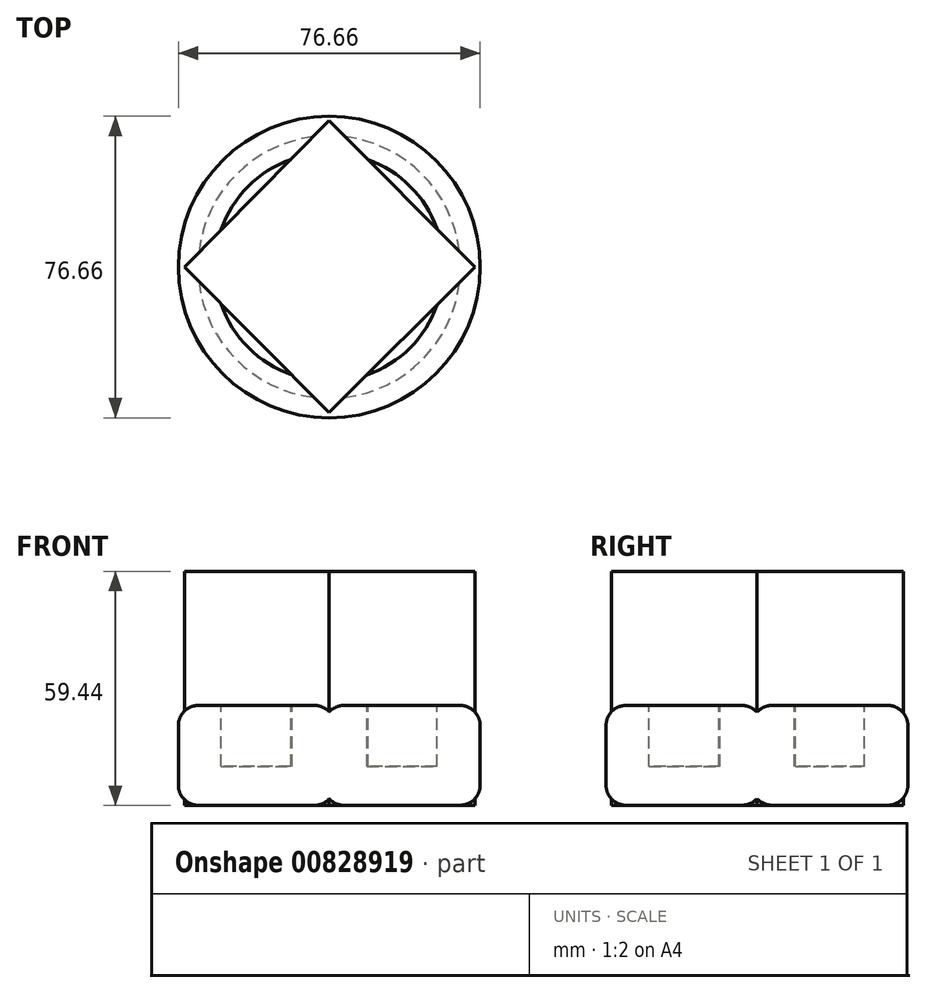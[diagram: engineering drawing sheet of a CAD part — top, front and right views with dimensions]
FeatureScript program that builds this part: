
annotation { "Feature Type Name" : "Feature", "Feature Type Description" : "" }
export const myFeature = defineFeature(function(context is Context, id is Id, definition is map)
    precondition{}
    {
        {
            var Q0;
            Q0=qCreatedBy(makeId("Top.planeOp"),FACE);
            var sketch = newSketch(context, id + "F0", { "sketchPlane" : qUnion([Q0])});
            skCircle(sketch, "E0", {"center": v(0, 0) * mm, "radius": 38.33 * mm});
            skSolve(sketch);
        }
        {
            var Q0;
            Q0=makeQuery(id+"F0.imprint","IMPRINT",FACE,{"disambiguationData":[TD([[makeQuery(id+"F0.imprint","IMPRINT",EDGE,{"derivedFrom":sQuery(id+"F0.wireOp",EDGE,"E0")}),1.0]])]});
            extrude(context, id + "F1", {"entities" : qUnion([Q0]), "depth" : 25.4 * mm, "offsetDistance" : 25.4 * mm});
        }
        {
            var Q0;
            Q0=makeQuery(id+"F1.opExtrude","CAP_EDGE",EDGE,{"disambiguationData":[OSD([sQuery(id+"F0.wireOp",EDGE,"E0")])],"isStart":false});
            var Q1;
            Q1=makeQuery(id+"F1.opExtrude","CAP_EDGE",EDGE,{"disambiguationData":[OSD([sQuery(id+"F0.wireOp",EDGE,"E0")])],"isStart":true});
            fillet(context, id + "F2", {"entities" : qUnion([Q0, Q1]), "radius" : 5.08 * mm, "tangentPropagation" : true, "allowEdgeOverflow" : false});
        }
        {
            var Q0;
            Q0=makeQuery(id+"F1.opExtrude","CAP_FACE",FACE,{"disambiguationData":[OSD([sQuery(id+"F0.wireOp",EDGE,"E0")])],"isStart":false});
            var sketch = newSketch(context, id + "F3", { "sketchPlane" : qUnion([Q0])});
            skCircle(sketch, "E1", {"center": v(0, 0) * mm, "radius": 29.03 * mm});
            skSolve(sketch);
        }
        {
            var Q0;
            Q0=makeQuery(id+"F3.imprint","IMPRINT",FACE,{"disambiguationData":[TD([[makeQuery(id+"F3.imprint","IMPRINT",EDGE,{"derivedFrom":sQuery(id+"F3.wireOp",EDGE,"E1")}),1.0]])]});
            extrude(context, id + "F4", {"entities" : qUnion([Q0]), "operationType" : NewBodyOperationType.REMOVE, "oppositeDirection" : true, "depth" : 44.2 * mm, "offsetDistance" : 25.4 * mm});
        }
        {
            var Q0;
            Q0=makeQuery(id+"F4.boolean.opBoolean","COPY",EDGE,{"derivedFrom":makeQuery(id+"F4.opExtrude","CAP_EDGE",EDGE,{"disambiguationData":[OSD([sQuery(id+"F3.wireOp",EDGE,"E1")])],"isStart":true})});
            var Q1;
            Q1=makeQuery(id+"F4.boolean.opBoolean","INTERSECT",EDGE,{"derivedFrom":[makeQuery(id+"F1.opExtrude","CAP_FACE",FACE,{"disambiguationData":[OSD([sQuery(id+"F0.wireOp",EDGE,"E0")])],"isStart":true}),makeQuery(id+"F4.opExtrude","SWEPT_FACE",FACE,{"disambiguationData":[OSD([sQuery(id+"F3.wireOp",EDGE,"E1")])]})]});
            fillet(context, id + "F5", {"entities" : qUnion([Q0, Q1]), "radius" : 5.08 * mm, "tangentPropagation" : true, "allowEdgeOverflow" : false});
        }
        {
            var Q0;
            Q0=qCreatedBy(makeId("Top.planeOp"),FACE);
            var sketch = newSketch(context, id + "F6", { "sketchPlane" : qUnion([Q0])});
            skCircle(sketch, "E2", {"center": v(0, 0) * mm, "radius": 21.2 * mm});
            skCircle(sketch, "E3", {"center": v(0, 0) * mm, "radius": 15.45 * mm});
            skCircle(sketch, "E4", {"center": v(0, 0) * mm, "radius": 24.98 * mm});
            skCircle(sketch, "E5", {"center": v(0, 0) * mm, "radius": 11.4 * mm});
            skCircle(sketch, "E6", {"center": v(0, 0) * mm, "radius": 7.3 * mm});
            skCircle(sketch, "E7", {"center": v(0, 0.63) * mm, "radius": 4.43 * mm});
            skSolve(sketch);
        }
        {
            var Q0;
            Q0=sQuery(id+"F6.wireOp",EDGE,"E4");
            var Q1;
            Q1=sQuery(id+"F6.wireOp",EDGE,"E2");
            var Q2;
            Q2=sQuery(id+"F6.wireOp",EDGE,"E3");
            var Q3;
            Q3=sQuery(id+"F6.wireOp",EDGE,"E5");
            var Q4;
            Q4=sQuery(id+"F6.wireOp",EDGE,"E6");
            var Q5;
            Q5=sQuery(id+"F6.wireOp",EDGE,"E7");
            extrude(context, id + "F7", {"bodyType" : ToolBodyType.SURFACE, "surfaceEntities" : qUnion([Q0, Q1, Q2, Q3, Q4, Q5]), "depth" : 25.4 * mm, "offsetDistance" : 25.4 * mm});
        }
        {
            var Q0;
            Q0=qCreatedBy(makeId("Top.planeOp"),FACE);
            var sketch = newSketch(context, id + "F8", { "sketchPlane" : qUnion([Q0])});
            skCircle(sketch, "E8", {"center": v(0, 0) * mm, "radius": 33.34 * mm});
            skSolve(sketch);
        }
        {
            var Q0;
            Q0=makeQuery(id+"F8.imprint","IMPRINT",FACE,{"disambiguationData":[TD([[makeQuery(id+"F8.imprint","IMPRINT",EDGE,{"derivedFrom":sQuery(id+"F8.wireOp",EDGE,"E8")}),1.0]])]});
            extrude(context, id + "F9", {"entities" : qUnion([Q0]), "operationType" : NewBodyOperationType.ADD, "depth" : 9.9 * mm, "offsetDistance" : 25.4 * mm});
        }
        {
            var Q0;
            Q0=qCreatedBy(makeId("Top.planeOp"),FACE);
            var sketch = newSketch(context, id + "F10", { "sketchPlane" : qUnion([Q0])});
            skLineSegment(sketch, "E9", {"start": v(0, 0) * mm, "end": v(0, 37.2) * mm});
            skLineSegment(sketch, "E10", {"start": v(0, 37.2) * mm, "end": v(37.07, 0) * mm});
            skLineSegment(sketch, "E11", {"start": v(37.07, 0) * mm, "end": v(0, -36.95) * mm});
            skLineSegment(sketch, "E12", {"start": v(0, -36.95) * mm, "end": v(-36.82, 0) * mm});
            skLineSegment(sketch, "E13", {"start": v(-36.82, 0) * mm, "end": v(0, 37.2) * mm});
            skSolve(sketch);
        }
        {
            var Q0;
            Q0=makeQuery(id+"F10.imprint","IMPRINT",FACE,{"disambiguationData":[TD([[makeQuery(id+"F10.imprint","IMPRINT",EDGE,{"derivedFrom":sQuery(id+"F10.wireOp",EDGE,"E10")}),-1.0]])]});
            extrude(context, id + "F11", {"entities" : qUnion([Q0]), "operationType" : NewBodyOperationType.ADD, "depth" : 59.44 * mm, "offsetDistance" : 25.4 * mm});
        }
    });
